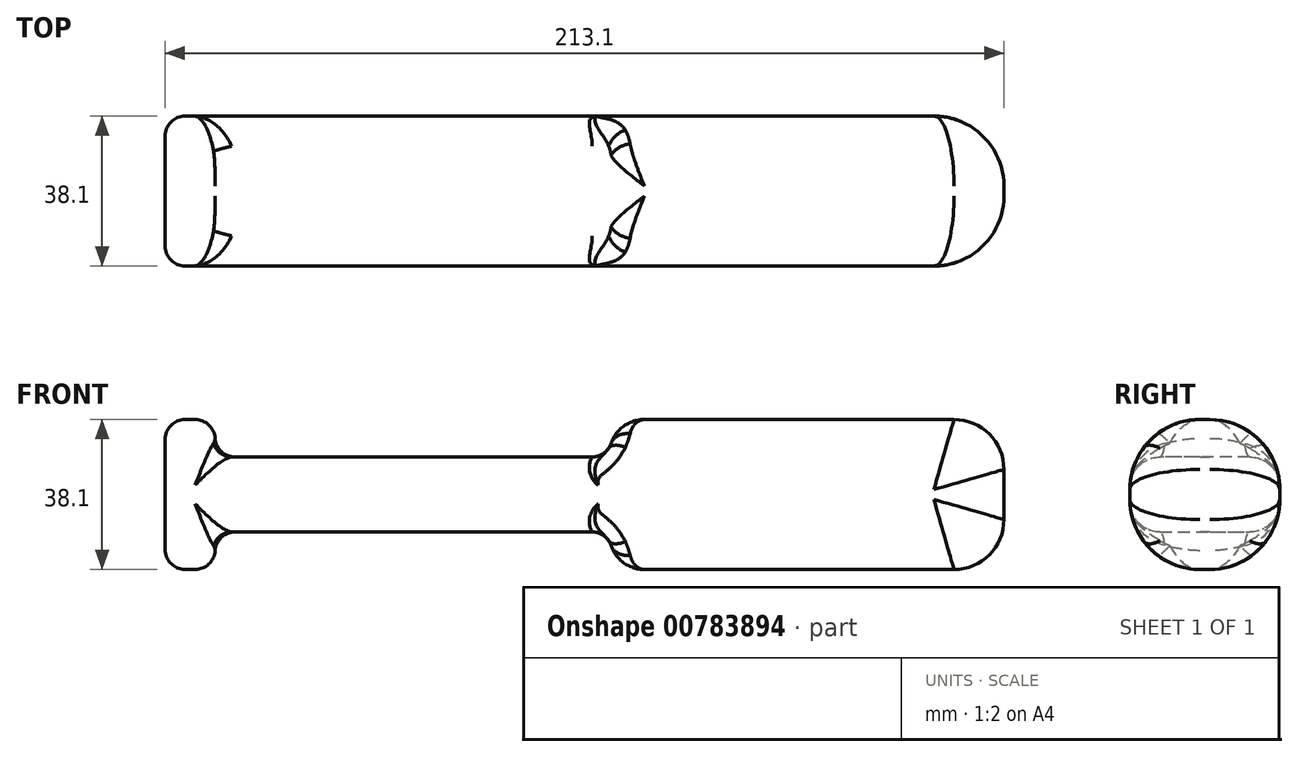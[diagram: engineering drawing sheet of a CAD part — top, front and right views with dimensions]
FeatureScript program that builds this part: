
annotation { "Feature Type Name" : "Feature", "Feature Type Description" : "" }
export const myFeature = defineFeature(function(context is Context, id is Id, definition is map)
    precondition{}
    {
        {
            var Q0;
            Q0=qCreatedBy(makeId("Front.planeOp"),FACE);
            var sketch = newSketch(context, id + "F0", { "sketchPlane" : qUnion([Q0])});
            skLineSegment(sketch, "E0", {"start": v(0.13, 49.8) * mm, "end": v(78.8, 49.8) * mm});
            skLineSegment(sketch, "E1", {"start": v(0.13, 11.7) * mm, "end": v(78.8, 11.7) * mm});
            skLineSegment(sketch, "E2", {"start": v(91.5, 37.1) * mm, "end": v(91.5, 24.4) * mm});
            skLineSegment(sketch, "E3", {"start": v(-8.76, 21.23) * mm, "end": v(-8.76, 20.6) * mm});
            skLineSegment(sketch, "E4", {"start": v(-8.76, 40.28) * mm, "end": v(-8.76, 40.92) * mm});
            skLineSegment(sketch, "E5", {"start": v(-8.76, 40.28) * mm, "end": v(-108.9, 40.28) * mm});
            skLineSegment(sketch, "E6", {"start": v(-8.76, 21.23) * mm, "end": v(-108.9, 21.23) * mm});
            skPoint(sketch, "E7.orphan", {"position": v(-8.76, 30.76) * mm});
            skPoint(sketch, "E8.orphan", {"position": v(-108.9, 49.8) * mm});
            skPoint(sketch, "E9.orphan", {"position": v(-108.9, 11.7) * mm});
            skPoint(sketch, "E10.visualSharp", {"position": v(-8.76, 49.8) * mm});
            skArc(sketch, "E10.filletArc", {"start": v(0.13, 49.8) * mm, "mid": v(-6.16, 47.2) * mm, "end": v(-8.76, 40.92) * mm});
            skPoint(sketch, "E11.visualSharp", {"position": v(-8.76, 11.7) * mm});
            skArc(sketch, "E11.filletArc", {"start": v(-8.76, 20.6) * mm, "mid": v(-6.16, 14.31) * mm, "end": v(0.13, 11.7) * mm});
            skPoint(sketch, "E12.visualSharp", {"position": v(91.5, 11.7) * mm});
            skArc(sketch, "E12.filletArc", {"start": v(78.8, 11.7) * mm, "mid": v(87.79, 15.43) * mm, "end": v(91.5, 24.4) * mm});
            skPoint(sketch, "E13.visualSharp", {"position": v(91.5, 49.8) * mm});
            skArc(sketch, "E13.filletArc", {"start": v(91.5, 37.1) * mm, "mid": v(87.79, 46.09) * mm, "end": v(78.8, 49.8) * mm});
            skLineSegment(sketch, "E14", {"start": v(-108.9, 49.8) * mm, "end": v(-108.9, 40.28) * mm});
            skLineSegment(sketch, "E15", {"start": v(-108.9, 11.7) * mm, "end": v(-121.6, 11.7) * mm});
            skLineSegment(sketch, "E16", {"start": v(-121.6, 11.7) * mm, "end": v(-121.6, 49.8) * mm});
            skLineSegment(sketch, "E17", {"start": v(-121.6, 49.8) * mm, "end": v(-108.9, 49.8) * mm});
            skLineSegment(sketch, "E18.trimOffspring", {"start": v(-108.9, 21.23) * mm, "end": v(-108.9, 11.7) * mm});
            skSolve(sketch);
        }
        {
            var Q0;
            Q0=makeQuery(id+"F0.imprint","IMPRINT",FACE,{"disambiguationData":[TD([[makeQuery(id+"F0.imprint","IMPRINT",EDGE,{"derivedFrom":sQuery(id+"F0.wireOp",EDGE,"E0")}),-1.0]])]});
            extrude(context, id + "F1", {"entities" : qUnion([Q0]), "depth" : 38.1 * mm, "offsetDistance" : 25.4 * mm});
        }
        {
            var Q0;
            Q0=makeQuery(id+"F1.opExtrude","CAP_EDGE",EDGE,{"disambiguationData":[OSD([sQuery(id+"F0.wireOp",EDGE,"E0")])],"isStart":false});
            var Q1;
            Q1=makeQuery(id+"F1.opExtrude","CAP_EDGE",EDGE,{"disambiguationData":[OSD([sQuery(id+"F0.wireOp",EDGE,"E0")])],"isStart":true});
            fillet(context, id + "F2", {"entities" : qUnion([Q0, Q1]), "radius" : 17.78 * mm, "tangentPropagation" : true, "allowEdgeOverflow" : false});
        }
        {
            var Q0;
            Q0=makeQuery(id+"F2.opFillet","BLEND_EDGE",EDGE,{"blendedFrom":[makeQuery(id+"F1.opExtrude","CAP_EDGE",EDGE,{"disambiguationData":[OSD([sQuery(id+"F0.wireOp",EDGE,"E0")])],"isStart":false}),makeQuery(id+"F1.opExtrude","SWEPT_FACE",FACE,{"disambiguationData":[OSD([sQuery(id+"F0.wireOp",EDGE,"E5")])]})],"blendedInto":[makeQuery(id+"F1.opExtrude","SWEPT_FACE",FACE,{"disambiguationData":[OSD([sQuery(id+"F0.wireOp",EDGE,"E5")])]})]});
            var Q1;
            Q1=makeQuery(id+"F2.opFillet","BLEND_EDGE",EDGE,{"blendedFrom":[makeQuery(id+"F1.opExtrude","CAP_EDGE",EDGE,{"disambiguationData":[OSD([sQuery(id+"F0.wireOp",EDGE,"E0")])],"isStart":true}),makeQuery(id+"F1.opExtrude","SWEPT_FACE",FACE,{"disambiguationData":[OSD([sQuery(id+"F0.wireOp",EDGE,"E5")])]})],"blendedInto":[makeQuery(id+"F1.opExtrude","SWEPT_FACE",FACE,{"disambiguationData":[OSD([sQuery(id+"F0.wireOp",EDGE,"E5")])]})]});
            var Q2;
            Q2=makeQuery(id+"F2.opFillet","BLEND_EDGE",EDGE,{"blendedFrom":[makeQuery(id+"F1.opExtrude","CAP_EDGE",EDGE,{"disambiguationData":[OSD([sQuery(id+"F0.wireOp",EDGE,"E1")])],"isStart":true}),makeQuery(id+"F1.opExtrude","SWEPT_FACE",FACE,{"disambiguationData":[OSD([sQuery(id+"F0.wireOp",EDGE,"E6")])]})],"blendedInto":[makeQuery(id+"F1.opExtrude","SWEPT_FACE",FACE,{"disambiguationData":[OSD([sQuery(id+"F0.wireOp",EDGE,"E6")])]})]});
            var Q3;
            Q3=makeQuery(id+"F2.opFillet","BLEND_EDGE",EDGE,{"blendedFrom":[makeQuery(id+"F1.opExtrude","CAP_EDGE",EDGE,{"disambiguationData":[OSD([sQuery(id+"F0.wireOp",EDGE,"E1")])],"isStart":false}),makeQuery(id+"F1.opExtrude","SWEPT_FACE",FACE,{"disambiguationData":[OSD([sQuery(id+"F0.wireOp",EDGE,"E6")])]})],"blendedInto":[makeQuery(id+"F1.opExtrude","SWEPT_FACE",FACE,{"disambiguationData":[OSD([sQuery(id+"F0.wireOp",EDGE,"E6")])]})]});
            fillet(context, id + "F3", {"entities" : qUnion([Q0, Q1, Q2, Q3]), "radius" : 7.62 * mm, "tangentPropagation" : true, "allowEdgeOverflow" : false});
        }
        {
            var Q0;
            Q0=makeQuery(id+"F2.opFillet","BLEND_EDGE",EDGE,{"blendedFrom":[makeQuery(id+"F1.opExtrude","CAP_EDGE",EDGE,{"disambiguationData":[OSD([sQuery(id+"F0.wireOp",EDGE,"E0")])],"isStart":false}),makeQuery(id+"F1.opExtrude","SWEPT_FACE",FACE,{"disambiguationData":[OSD([sQuery(id+"F0.wireOp",EDGE,"E14")])]})],"blendedInto":[makeQuery(id+"F1.opExtrude","SWEPT_FACE",FACE,{"disambiguationData":[OSD([sQuery(id+"F0.wireOp",EDGE,"E14")])]})]});
            var Q1;
            Q1=makeQuery(id+"F2.opFillet","BLEND_EDGE",EDGE,{"blendedFrom":[makeQuery(id+"F1.opExtrude","CAP_EDGE",EDGE,{"disambiguationData":[OSD([sQuery(id+"F0.wireOp",EDGE,"E1")])],"isStart":false}),makeQuery(id+"F1.opExtrude","SWEPT_FACE",FACE,{"disambiguationData":[OSD([sQuery(id+"F0.wireOp",EDGE,"E18.trimOffspring")])]})],"blendedInto":[makeQuery(id+"F1.opExtrude","SWEPT_FACE",FACE,{"disambiguationData":[OSD([sQuery(id+"F0.wireOp",EDGE,"E18.trimOffspring")])]})]});
            var Q2;
            Q2=makeQuery(id+"F2.opFillet","BLEND_EDGE",EDGE,{"blendedFrom":[makeQuery(id+"F1.opExtrude","CAP_EDGE",EDGE,{"disambiguationData":[OSD([sQuery(id+"F0.wireOp",EDGE,"E0")])],"isStart":false}),makeQuery(id+"F1.opExtrude","SWEPT_FACE",FACE,{"disambiguationData":[OSD([sQuery(id+"F0.wireOp",EDGE,"E16")])]})],"blendedInto":[makeQuery(id+"F1.opExtrude","SWEPT_FACE",FACE,{"disambiguationData":[OSD([sQuery(id+"F0.wireOp",EDGE,"E16")])]})]});
            fillet(context, id + "F4", {"entities" : qUnion([Q0, Q1, Q2]), "radius" : 5.08 * mm, "tangentPropagation" : true, "allowEdgeOverflow" : false});
        }
        {
            var Q0;
            Q0=makeQuery(id+"F1.opExtrude","SWEPT_EDGE",EDGE,{"disambiguationData":[OSD([sQuery(id+"F0.wireOp",EDGE,"E5"),sQuery(id+"F0.wireOp",EDGE,"E14")])]});
            var Q1;
            Q1=makeQuery(id+"F1.opExtrude","SWEPT_EDGE",EDGE,{"disambiguationData":[OSD([sQuery(id+"F0.wireOp",EDGE,"E6"),sQuery(id+"F0.wireOp",EDGE,"E18.trimOffspring")])]});
            fillet(context, id + "F5", {"entities" : qUnion([Q0, Q1]), "radius" : 5.08 * mm, "tangentPropagation" : true, "allowEdgeOverflow" : false});
        }
        {
            var Q0;
            Q0=makeQuery(id+"F1.opExtrude","SWEPT_EDGE",EDGE,{"disambiguationData":[OSD([sQuery(id+"F0.wireOp",EDGE,"E4"),sQuery(id+"F0.wireOp",EDGE,"E5")])]});
            var Q1;
            Q1=makeQuery(id+"F2.opFillet","BLEND_EDGE",EDGE,{"blendedFrom":[makeQuery(id+"F1.opExtrude","CAP_EDGE",EDGE,{"disambiguationData":[OSD([sQuery(id+"F0.wireOp",EDGE,"E0")])],"isStart":false}),makeQuery(id+"F1.opExtrude","SWEPT_FACE",FACE,{"disambiguationData":[OSD([sQuery(id+"F0.wireOp",EDGE,"E10.filletArc")])]})],"blendedInto":[makeQuery(id+"F1.opExtrude","SWEPT_FACE",FACE,{"disambiguationData":[OSD([sQuery(id+"F0.wireOp",EDGE,"E10.filletArc")])]})]});
            var Q2;
            Q2=makeQuery(id+"F2.opFillet","BLEND_EDGE",EDGE,{"blendedFrom":[makeQuery(id+"F1.opExtrude","CAP_EDGE",EDGE,{"disambiguationData":[OSD([sQuery(id+"F0.wireOp",EDGE,"E0")])],"isStart":true}),makeQuery(id+"F1.opExtrude","SWEPT_FACE",FACE,{"disambiguationData":[OSD([sQuery(id+"F0.wireOp",EDGE,"E10.filletArc")])]})],"blendedInto":[makeQuery(id+"F1.opExtrude","SWEPT_FACE",FACE,{"disambiguationData":[OSD([sQuery(id+"F0.wireOp",EDGE,"E10.filletArc")])]})]});
            fillet(context, id + "F6", {"entities" : qUnion([Q0, Q1, Q2]), "radius" : 5.08 * mm, "tangentPropagation" : true, "allowEdgeOverflow" : false});
        }
        {
            var Q0;
            Q0=makeQuery(id+"F1.opExtrude","SWEPT_EDGE",EDGE,{"disambiguationData":[OSD([sQuery(id+"F0.wireOp",EDGE,"E3"),sQuery(id+"F0.wireOp",EDGE,"E11.filletArc")])]});
            var Q1;
            Q1=makeQuery(id+"F1.opExtrude","SWEPT_EDGE",EDGE,{"disambiguationData":[OSD([sQuery(id+"F0.wireOp",EDGE,"E3"),sQuery(id+"F0.wireOp",EDGE,"E6")])]});
            var Q2;
            Q2=makeQuery(id+"F2.opFillet","BLEND_EDGE",EDGE,{"blendedFrom":[makeQuery(id+"F1.opExtrude","CAP_EDGE",EDGE,{"disambiguationData":[OSD([sQuery(id+"F0.wireOp",EDGE,"E1")])],"isStart":false}),makeQuery(id+"F1.opExtrude","SWEPT_FACE",FACE,{"disambiguationData":[OSD([sQuery(id+"F0.wireOp",EDGE,"E11.filletArc")])]})],"blendedInto":[makeQuery(id+"F1.opExtrude","SWEPT_FACE",FACE,{"disambiguationData":[OSD([sQuery(id+"F0.wireOp",EDGE,"E11.filletArc")])]})]});
            var Q3;
            Q3=makeQuery(id+"F2.opFillet","BLEND_EDGE",EDGE,{"blendedFrom":[makeQuery(id+"F1.opExtrude","CAP_EDGE",EDGE,{"disambiguationData":[OSD([sQuery(id+"F0.wireOp",EDGE,"E1")])],"isStart":true}),makeQuery(id+"F1.opExtrude","SWEPT_FACE",FACE,{"disambiguationData":[OSD([sQuery(id+"F0.wireOp",EDGE,"E11.filletArc")])]})],"blendedInto":[makeQuery(id+"F1.opExtrude","SWEPT_FACE",FACE,{"disambiguationData":[OSD([sQuery(id+"F0.wireOp",EDGE,"E11.filletArc")])]})]});
            fillet(context, id + "F7", {"entities" : qUnion([Q0, Q1, Q2, Q3]), "radius" : 5.08 * mm, "tangentPropagation" : true, "allowEdgeOverflow" : false});
        }
    });
